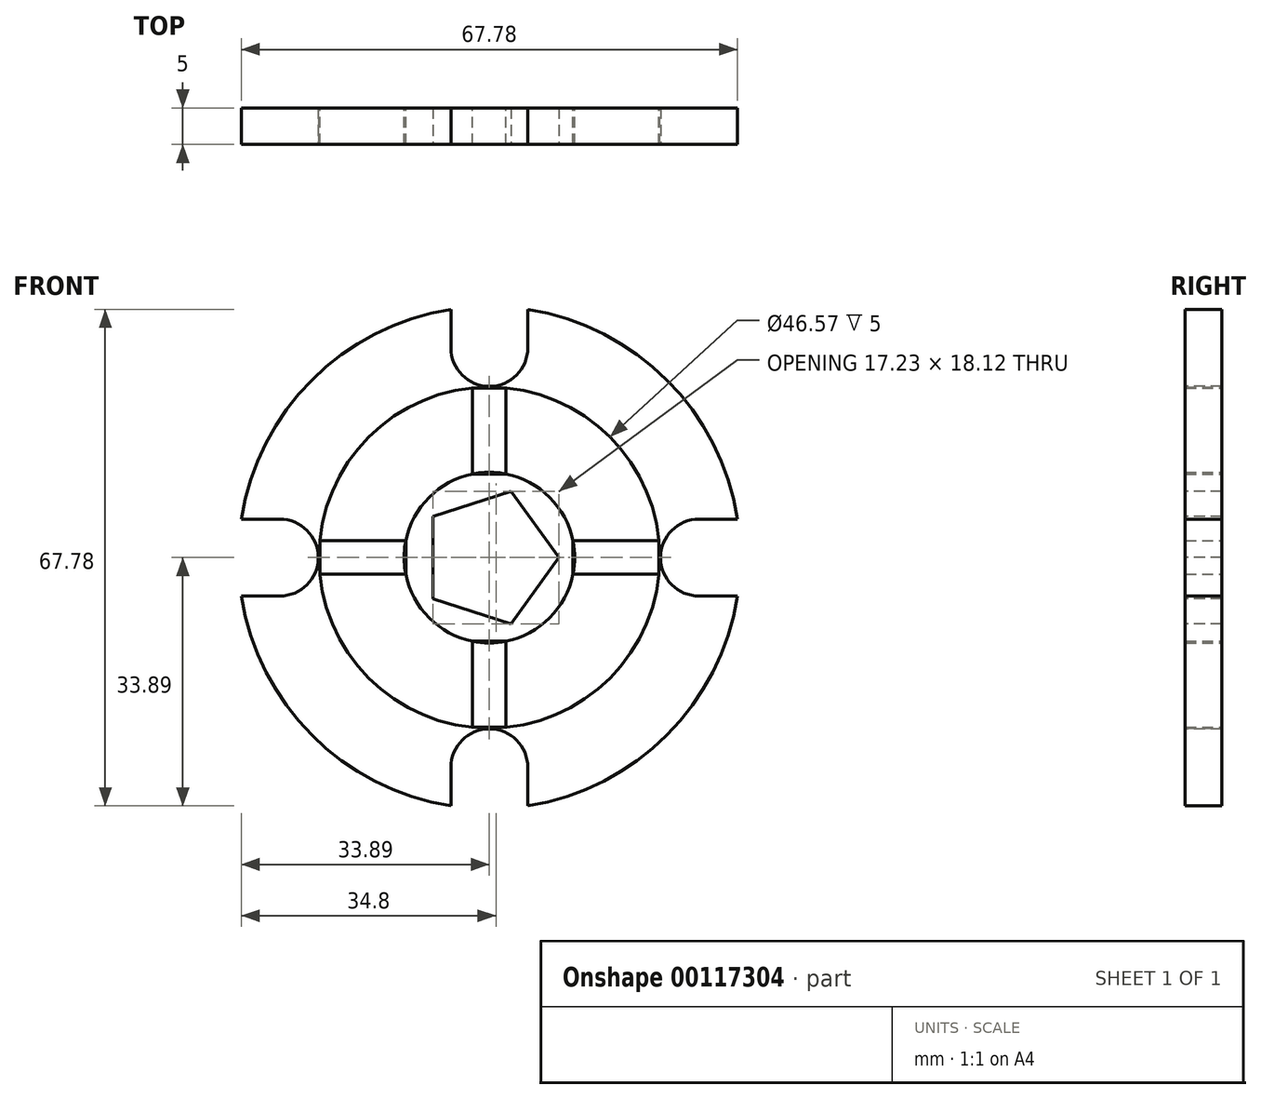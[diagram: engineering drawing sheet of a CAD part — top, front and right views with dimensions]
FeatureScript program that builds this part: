
annotation { "Feature Type Name" : "Feature", "Feature Type Description" : "" }
export const myFeature = defineFeature(function(context is Context, id is Id, definition is map)
    precondition{}
    {
        {
            var Q0;
            Q0=qCreatedBy(makeId("Front.planeOp"),FACE);
            var sketch = newSketch(context, id + "F0", { "sketchPlane" : qUnion([Q0])});
            skCircle(sketch, "E0", {"center": v(0, 0) * mm, "radius": 34.3 * mm});
            skCircle(sketch, "E1", {"center": v(0, 0) * mm, "radius": 11.64 * mm});
            skCircle(sketch, "E2", {"center": v(0, 0) * mm, "radius": 23.28 * mm});
            skLineSegment(sketch, "E3.bottom", {"start": v(-23.17, 2.29) * mm, "end": v(-11.42, 2.29) * mm});
            skLineSegment(sketch, "E3.top", {"start": v(-23.17, -2.29) * mm, "end": v(-11.42, -2.29) * mm});
            skLineSegment(sketch, "E3.left", {"start": v(-23.17, 2.29) * mm, "end": v(-23.17, -2.29) * mm});
            skLineSegment(sketch, "E3.right", {"start": v(-11.42, 2.29) * mm, "end": v(-11.42, -2.29) * mm});
            skPoint(sketch, "E3.middle", {"position": v(-17.3, 0) * mm});
            skLineSegment(sketch, "E4.bottom", {"start": v(11.42, 2.29) * mm, "end": v(23.17, 2.29) * mm});
            skLineSegment(sketch, "E4.top", {"start": v(11.42, -2.29) * mm, "end": v(23.17, -2.29) * mm});
            skLineSegment(sketch, "E4.left", {"start": v(11.42, 2.29) * mm, "end": v(11.42, -2.29) * mm});
            skLineSegment(sketch, "E4.right", {"start": v(23.17, 2.29) * mm, "end": v(23.17, -2.29) * mm});
            skPoint(sketch, "E4.middle", {"position": v(17.3, 0) * mm});
            skLineSegment(sketch, "E5.bottom", {"start": v(-2.29, 23.17) * mm, "end": v(2.29, 23.17) * mm});
            skLineSegment(sketch, "E5.top", {"start": v(-2.29, 11.39) * mm, "end": v(2.29, 11.39) * mm});
            skLineSegment(sketch, "E5.left", {"start": v(-2.29, 23.17) * mm, "end": v(-2.29, 11.39) * mm});
            skLineSegment(sketch, "E5.right", {"start": v(2.29, 23.17) * mm, "end": v(2.29, 11.39) * mm});
            skPoint(sketch, "E5.middle", {"position": v(0, 17.28) * mm});
            skLineSegment(sketch, "E6.bottom", {"start": v(-2.29, -11.42) * mm, "end": v(2.29, -11.42) * mm});
            skLineSegment(sketch, "E6.top", {"start": v(-2.29, -23.17) * mm, "end": v(2.29, -23.17) * mm});
            skLineSegment(sketch, "E6.left", {"start": v(-2.29, -11.42) * mm, "end": v(-2.29, -23.17) * mm});
            skLineSegment(sketch, "E6.right", {"start": v(2.29, -11.42) * mm, "end": v(2.29, -23.17) * mm});
            skPoint(sketch, "E6.middle", {"position": v(0, -17.3) * mm});
            skSolve(sketch);
        }
        {
            var Q0;
            {var subQ1=sQuery(id+"F0.wireOp",EDGE,"E3.bottom");Q0=makeQuery(id+"F0.imprint","IMPRINT",FACE,{"disambiguationData":[TD([[makeQuery(id+"F0.imprint","IMPRINT",EDGE,{"derivedFrom":subQ1}),-1.0]])]});}
            var Q1;
            {var subQ6=sQuery(id+"F0.wireOp",EDGE,"E3.right");Q1=makeQuery(id+"F0.imprint","IMPRINT",FACE,{"disambiguationData":[TD([[makeQuery(id+"F0.imprint","IMPRINT",EDGE,{"derivedFrom":subQ6}),1.0]])]});}
            var Q2;
            {var subQ5=sQuery(id+"F0.wireOp",EDGE,"E5.bottom");Q2=makeQuery(id+"F0.imprint","IMPRINT",FACE,{"disambiguationData":[TD([[makeQuery(id+"F0.imprint","IMPRINT",EDGE,{"derivedFrom":subQ5}),-1.0]])]});}
            var Q3;
            {var subQ1=sQuery(id+"F0.wireOp",EDGE,"E4.bottom");Q3=makeQuery(id+"F0.imprint","IMPRINT",FACE,{"disambiguationData":[TD([[makeQuery(id+"F0.imprint","IMPRINT",EDGE,{"derivedFrom":subQ1}),-1.0]])]});}
            var Q4;
            Q4=makeQuery(id+"F0.imprint","IMPRINT",FACE,{"disambiguationData":[TD([[makeQuery(id+"F0.imprint","IMPRINT",EDGE,{"derivedFrom":sQuery(id+"F0.wireOp",EDGE,"E6.top")}),1.0]])]});
            var Q5;
            Q5=makeQuery(id+"F0.imprint","IMPRINT",FACE,{"disambiguationData":[TD([[makeQuery(id+"F0.imprint","IMPRINT",EDGE,{"derivedFrom":sQuery(id+"F0.wireOp",EDGE,"E0")}),1.0]])]});
            extrude(context, id + "F1", {"entities" : qUnion([Q0, Q1, Q2, Q3, Q4, Q5]), "depth" : 5 * mm});
        }
        {
            var Q0;
            Q0=makeQuery(id+"F1.opExtrude","CAP_FACE",FACE,{"disambiguationData":[OSD([sQuery(id+"F0.wireOp",EDGE,"E0"),sQuery(id+"F0.wireOp",EDGE,"E2")])],"isStart":false});
            var sketch = newSketch(context, id + "F2", { "sketchPlane" : qUnion([Q0])});
            skArc(sketch, "E7", {"start": v(5.25, -28.63) * mm, "mid": v(0, -23.38) * mm, "end": v(-5.25, -28.63) * mm});
            skLineSegment(sketch, "E8", {"start": v(5.25, -28.63) * mm, "end": v(5.25, -33.89) * mm});
            skLineSegment(sketch, "E9", {"start": v(-5.25, -28.63) * mm, "end": v(-5.25, -33.89) * mm});
            skLineSegment(sketch, "E10.MirrorCS", {"start": v(5.25, 28.63) * mm, "end": v(5.25, 33.89) * mm});
            skArc(sketch, "E11.1.0", {"start": v(28.63, 5.25) * mm, "mid": v(23.38, 0) * mm, "end": v(28.63, -5.25) * mm});
            skLineSegment(sketch, "E11.1.1", {"start": v(28.63, 5.25) * mm, "end": v(33.89, 5.25) * mm});
            skLineSegment(sketch, "E11.1.2", {"start": v(28.63, -5.25) * mm, "end": v(33.89, -5.25) * mm});
            skArc(sketch, "E11.2.0", {"start": v(-5.25, 28.63) * mm, "mid": v(0, 23.38) * mm, "end": v(5.25, 28.63) * mm});
            skLineSegment(sketch, "E11.2.1", {"start": v(-5.25, 28.63) * mm, "end": v(-5.25, 33.89) * mm});
            skArc(sketch, "E11.3.0", {"start": v(-28.63, -5.25) * mm, "mid": v(-23.38, 0) * mm, "end": v(-28.63, 5.25) * mm});
            skLineSegment(sketch, "E11.3.1", {"start": v(-28.63, -5.25) * mm, "end": v(-33.89, -5.25) * mm});
            skLineSegment(sketch, "E11.3.2", {"start": v(-28.63, 5.25) * mm, "end": v(-33.89, 5.25) * mm});
            skPoint(sketch, "E11.center", {"position": v(0, 0) * mm});
            skSolve(sketch);
        }
        {
            var Q0;
            Q0 = qSketchRegion(id + "F2", true);
            var Q1;
            Q1=makeQuery(id+"F2.imprint","IMPRINT",FACE,{"disambiguationData":[TD([[makeQuery(id+"F2.imprint","IMPRINT",EDGE,{"derivedFrom":sQuery(id+"F2.wireOp",EDGE,"E11.1.0")}),1.0]])]});
            var Q2;
            Q2=makeQuery(id+"F2.imprint","IMPRINT",FACE,{"disambiguationData":[TD([[makeQuery(id+"F2.imprint","IMPRINT",EDGE,{"derivedFrom":sQuery(id+"F2.wireOp",EDGE,"E7")}),1.0]])]});
            var Q3;
            Q3=makeQuery(id+"F2.imprint","IMPRINT",FACE,{"disambiguationData":[TD([[makeQuery(id+"F2.imprint","IMPRINT",EDGE,{"derivedFrom":sQuery(id+"F2.wireOp",EDGE,"E11.3.0")}),1.0]])]});
            var Q4;
            Q4=makeQuery(id+"F2.imprint","IMPRINT",FACE,{"disambiguationData":[TD([[makeQuery(id+"F2.imprint","IMPRINT",EDGE,{"derivedFrom":sQuery(id+"F2.wireOp",EDGE,"E11.2.0")}),1.0]])]});
            extrude(context, id + "F3", {"entities" : qUnion([Q0, Q1, Q2, Q3, Q4]), "operationType" : NewBodyOperationType.REMOVE, "endBound" : BoundingType.THROUGH_ALL, "oppositeDirection" : true, "depth" : 25.4 * mm});
        }
        {
            var Q0;
            Q0=makeQuery(id+"F1.opExtrude","CAP_FACE",FACE,{"disambiguationData":[OSD([sQuery(id+"F0.wireOp",EDGE,"E1"),sQuery(id+"F0.wireOp",EDGE,"E3.right"),sQuery(id+"F0.wireOp",EDGE,"E4.left"),sQuery(id+"F0.wireOp",EDGE,"E5.top"),sQuery(id+"F0.wireOp",EDGE,"E5.left"),sQuery(id+"F0.wireOp",EDGE,"E5.right"),sQuery(id+"F0.wireOp",EDGE,"E6.bottom")])],"isStart":false});
            var sketch = newSketch(context, id + "F4", { "sketchPlane" : qUnion([Q0])});
            skCircle(sketch, "E12.cCircle", {"center": v(0, 0) * mm, "radius": 9.53 * mm, "construction": true});
            skLineSegment(sketch, "E12.0", {"start": v(9.52, 0) * mm, "end": v(2.94, -9.06) * mm});
            skLineSegment(sketch, "E12.1", {"start": v(2.94, -9.06) * mm, "end": v(-7.7, -5.6) * mm});
            skLineSegment(sketch, "E12.2", {"start": v(-7.7, -5.6) * mm, "end": v(-7.7, 5.6) * mm});
            skLineSegment(sketch, "E12.3", {"start": v(-7.7, 5.6) * mm, "end": v(2.94, 9.06) * mm});
            skLineSegment(sketch, "E12.4", {"start": v(2.94, 9.06) * mm, "end": v(9.53, 0) * mm});
            skSolve(sketch);
        }
        {
            var Q0;
            Q0 = qSketchRegion(id + "F4", true);
            extrude(context, id + "F5", {"entities" : qUnion([Q0]), "operationType" : NewBodyOperationType.REMOVE, "endBound" : BoundingType.THROUGH_ALL, "oppositeDirection" : true, "depth" : 25.4 * mm});
        }
    });
